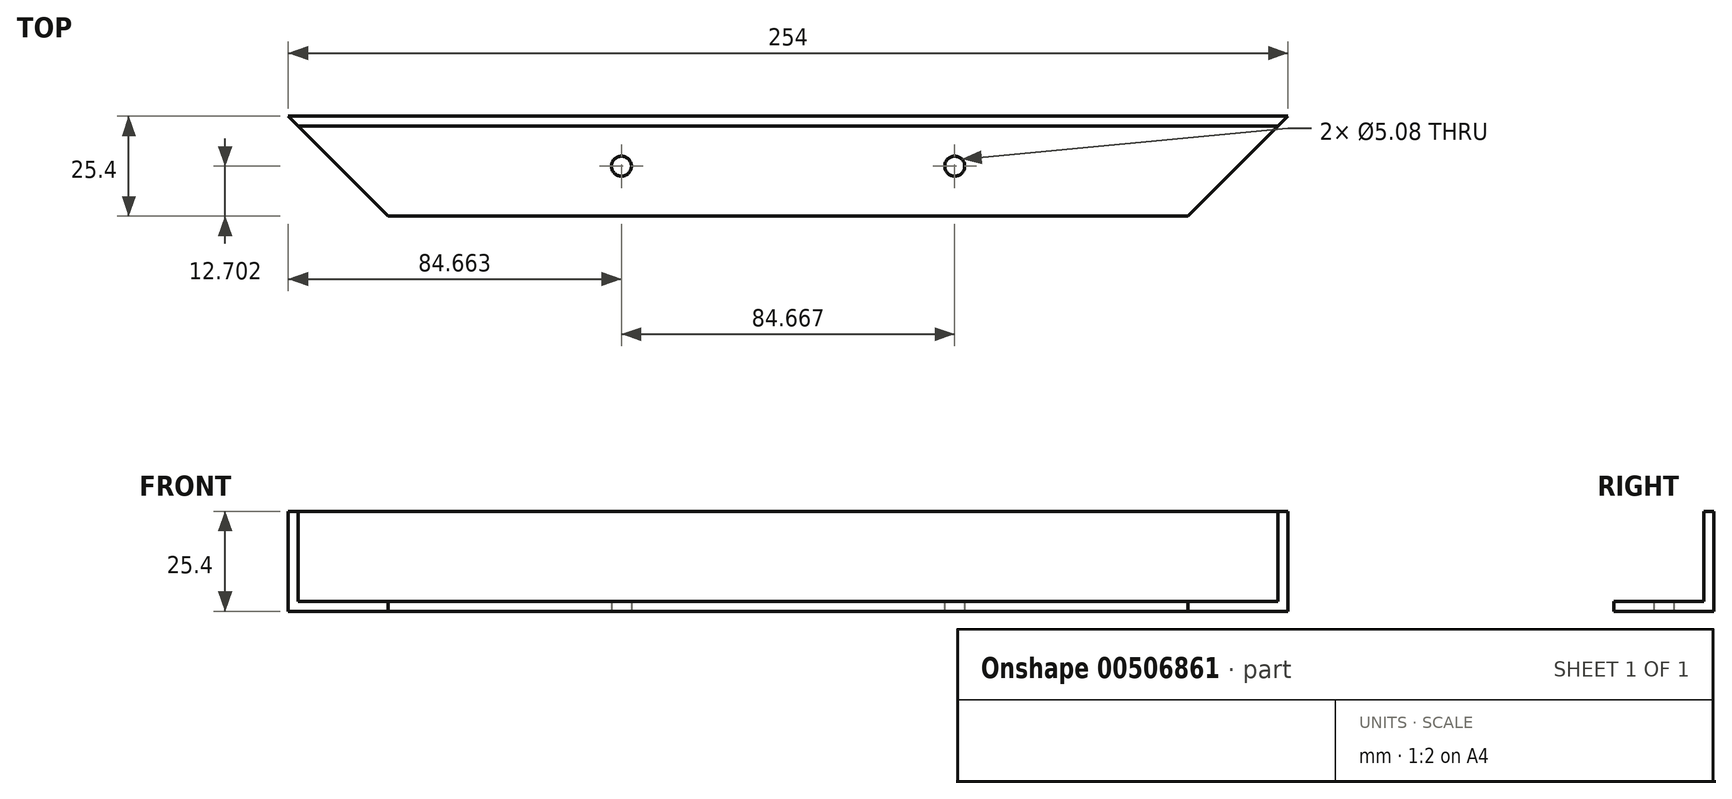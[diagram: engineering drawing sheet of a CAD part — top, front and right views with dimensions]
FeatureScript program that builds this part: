
annotation { "Feature Type Name" : "Feature", "Feature Type Description" : "" }
export const myFeature = defineFeature(function(context is Context, id is Id, definition is map)
    precondition{}
    {
        {
            var Q0;
            Q0=qCreatedBy(makeId("Top.planeOp"),FACE);
            var sketch = newSketch(context, id + "F0", { "sketchPlane" : qUnion([Q0])});
            skLineSegment(sketch, "E0.bottom", {"start": v(-169.33, 6.43) * mm, "end": v(84.67, 6.43) * mm});
            skLineSegment(sketch, "E0.top", {"start": v(-169.33, -18.97) * mm, "end": v(84.67, -18.97) * mm});
            skLineSegment(sketch, "E0.left", {"start": v(-169.33, 6.43) * mm, "end": v(-169.33, -18.97) * mm});
            skLineSegment(sketch, "E0.right", {"start": v(84.67, 6.43) * mm, "end": v(84.67, -18.97) * mm});
            skPoint(sketch, "E1", {"position": v(-143.93, -18.97) * mm});
            skPoint(sketch, "E2", {"position": v(59.27, -18.97) * mm});
            skLineSegment(sketch, "E3", {"start": v(84.67, 6.43) * mm, "end": v(59.27, -18.97) * mm});
            skLineSegment(sketch, "E4", {"start": v(-143.93, -18.97) * mm, "end": v(-169.33, 6.43) * mm});
            skPoint(sketch, "E5", {"position": v(-84.67, 6.43) * mm});
            skPoint(sketch, "E6", {"position": v(0, 6.43) * mm});
            skLineSegment(sketch, "E7", {"start": v(-84.67, 6.43) * mm, "end": v(-84.67, -18.97) * mm, "construction": true});
            skLineSegment(sketch, "E8", {"start": v(0, 6.43) * mm, "end": v(0, -18.97) * mm, "construction": true});
            skCircle(sketch, "E9", {"center": v(-84.67, -6.27) * mm, "radius": 2.54 * mm});
            skCircle(sketch, "E10", {"center": v(0, -6.27) * mm, "radius": 2.54 * mm});
            skSolve(sketch);
        }
        {
            var Q0;
            Q0=makeQuery(id+"F0.imprint","IMPRINT",FACE,{"disambiguationData":[TD([[makeQuery(id+"F0.imprint","IMPRINT",EDGE,{"derivedFrom":sQuery(id+"F0.wireOp",EDGE,"E0.bottom")}),-1.0]])]});
            extrude(context, id + "F1", {"entities" : qUnion([Q0]), "depth" : 25.4 * mm, "offsetDistance" : 25.4 * mm});
        }
        {
            var Q0;
            Q0=makeQuery(id+"F1.opExtrude","SWEPT_FACE",FACE,{"disambiguationData":[OSD([sQuery(id+"F0.wireOp",EDGE,"PSnNwnKP-KyGL-S50L-rR3s-k9mVRHxPJs2z")])]});
            var Q1;
            Q1=makeQuery(id+"F1.opExtrude","SWEPT_FACE",FACE,{"disambiguationData":[OSD([sQuery(id+"F0.wireOp",EDGE,"7DPQojG5-S4nv-vPj8-k88P-T7nccwHz7Moq")])]});
            var Q2;
            Q2=makeQuery(id+"F1.opExtrude","SWEPT_FACE",FACE,{"disambiguationData":[OSD([sQuery(id+"F0.wireOp",EDGE,"E3")])]});
            var Q3;
            Q3=makeQuery(id+"F1.opExtrude","SWEPT_FACE",FACE,{"disambiguationData":[OSD([sQuery(id+"F0.wireOp",EDGE,"E4")])]});
            var Q4;
            Q4=makeQuery(id+"F1.opExtrude","SWEPT_FACE",FACE,{"disambiguationData":[OSD([sQuery(id+"F0.wireOp",EDGE,"E0.top")])]});
            var Q5;
            Q5=makeQuery(id+"F1.opExtrude","CAP_FACE",FACE,{"disambiguationData":[OSD([sQuery(id+"F0.wireOp",EDGE,"E0.bottom"),sQuery(id+"F0.wireOp",EDGE,"E0.top"),sQuery(id+"F0.wireOp",EDGE,"E3"),sQuery(id+"F0.wireOp",EDGE,"E4"),sQuery(id+"F0.wireOp",EDGE,"E9"),sQuery(id+"F0.wireOp",EDGE,"E10")])],"isStart":false});
            var Q6;
            Q6=makeQuery(id+"F1.opExtrude","SWEPT_FACE",FACE,{"disambiguationData":[OSD([sQuery(id+"F0.wireOp",EDGE,"E9")])]});
            var Q7;
            Q7=makeQuery(id+"F1.opExtrude","SWEPT_FACE",FACE,{"disambiguationData":[OSD([sQuery(id+"F0.wireOp",EDGE,"E10")])]});
            shell(context, id + "F2", {"entities" : qUnion([Q0, Q1, Q2, Q3, Q4, Q5, Q6, Q7]), "thickness" : 2.54 * mm});
        }
    });
